FCSTD DOCUMENT  (FreeCAD 1.0R39109 (Git))
Label: Studs_Frame
License: All rights reserved
LicenseURL: http://en.wikipedia.org/wiki/All_rights_reserved
objects: App::Link×1, Part::FeaturePython×1, Spreadsheet::Sheet×1
EXTERNAL_REF file=Studs_Frame_Base.FCStd obj=Part
EXTERNAL_REF file=../../Master_of_Puppets.FCStd obj=Alternator
EXTERNAL_REF file=../../Master_of_Puppets.FCStd obj=Spreadsheet

FEATURE [App::Link] Link  label="Base"
  LinkPlacement = pos=(192.5,0,0) rot=(0,0,1;0rad)
  LinkedObject = -> <external Studs_Frame_Base.FCStd>#Part
  Placement = pos=(192.5,0,0) rot=(0,0,1;0rad)
  expr: .LinkPlacement.Base.x = Spreadsheet.CircumRadius
FEATURE [Part::FeaturePython] Array  label="Studs_Frame"  # Draft array (typed FeaturePython)
  AlwaysSyncPlacement = false
  Angle = 360
  ArrayType = 1
  Axis = (0,0,1)
  Base = -> Link
  Center = (0,0,0)
  Count = 3
  ExpandArray = false
  Fuse = false
  IntervalAxis = (0,0,0)
  IntervalX = (50,0,0)
  IntervalY = (0,50,0)
  IntervalZ = (0,0,50)
  NumberCircles = 3
  NumberPolar = 3
  NumberX = 2
  NumberY = 2
  NumberZ = 1
  Placement = pos=(0,0,-111.26) rot=(0,0,1;-0.523599rad)
  PlacementList = 3 placements: [(192.5,0,0),(-96.25,166.71,0),(-96.25,-166.71,0)]
  RadialDistance = 50
  ScaleList = (3) [(1,1,1),(1,1,1),(1,1,1)]
  Symmetry = 1
  TangentialDistance = 25
  expr: .Placement.Base.z = Spreadsheet.Z
  expr: .Placement.Rotation.Angle = Spreadsheet.Angle
  expr: NumberPolar = Spreadsheet.NumberOfStatorHoles
FEATURE [Spreadsheet::Sheet] Spreadsheet
  cells = A1='Inputs; A2='CalculatedWindTurbineShape; B2(CalculatedWindTurbineShape)==Master_of_Puppets#Spreadsheet.CalculatedWindTurbineShape; A3='StatorHolesCircumradius; B3(StatorHolesCircumradius)==Master_of_Puppets#Alternator.StatorHolesCircumradius; A4='StatorMountingStudsLength; B4(StatorMountingStudsLength)==Master_of_Puppets#Alternator.StatorMountingStudsLength; A5='CoilLegWidth; B5(CoilLegWidth)==Master_of_Puppets#Spreadsheet.CoilLegWidth; A6='Angle; A7='TShapeAngle; B7(TShapeAngle)==-30 deg; A8='HShapeAngle; B8(HShapeAngle)==45 deg; A9='StarShapeAngle; B9(StarShapeAngle)==60 deg; A10='Angle; B10(Angle)==CalculatedWindTurbineShape == <<T>> ? TShapeAngle : (CalculatedWindTurbineShape == <<H>> ? HShapeAngle : StarShapeAngle); A11='CircumRadius; B11(CircumRadius)==StatorHolesCircumradius; A12='NumberOfStatorHoles; B12(NumberOfStatorHoles)==Master_of_Puppets#Alternator.NumberOfStatorHoles; A13='Placement; A14='Z; B14(Z)==-StatorMountingStudsLength
